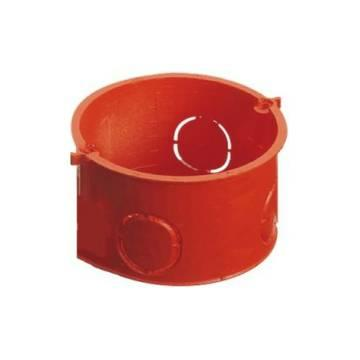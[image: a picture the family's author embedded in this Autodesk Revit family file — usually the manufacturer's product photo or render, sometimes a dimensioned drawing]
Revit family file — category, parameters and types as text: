
# Revit family: Building-ContenitoriIncasso-GEWISS-24SC-SCATOLE-INCASSO_TONDA
name_source: partatom
category: Apparecchi elettrici
revit_build: Autodesk Revit 2016 (Build: 20161004_0715(x64)
units: mm (PartAtom-declared; Revit-internal decimal feet)

## family parameters
Condiviso = Sì
Host = Muro
Mantenere orientamento annotazione = Sì
Numero OmniClass = 23.80.30.14.24
Punto di calcolo locali = Sì
Quota connettore circolare = Usa diametro
Sempre verticale = Sì
Taglio con vuoti quando caricato = Sì
Tipo di parte = Normale
Titolo OmniClass = Junction Boxes

## types (2) — shared parameters
Caratteristiche = Halogen free
Catalogo = BUILDING
Catalogo Serie = 24SC
Codice Electrocod = 0210
Descrizione: = Cilindrica
Diametro = 85 mm  [stored 0.278871 ft]
Diametro interno = 80 mm  [stored 0.262467 ft]
Glow Wire Test = 650°C
IDF = 002cb684-893c-4c20-b679-15194001214f
IDT = e9e05727-a289-4381-9e61-a78239658332
Immagine tipo = GW24210.jpg
Installazione = Incasso
Per Pareti = Muratura
Produttore = GEWISS S.p.A.
Profondità = 42 mm  [stored 0.137795 ft]
Profondità interna = 37 mm  [stored 0.121391 ft]
SEO = Scatola
Scheda Tecnica = https://www.gewiss.com
Temperatura di impiego = -15 +60 °C
Termopressione con biglia = 70 °C
URL = https://www.gewiss.com
Versione file RFA = 19.0

## per-type parameters (varying)
| type | Codice EAN | Descrizione | Dimensioni (mm) | Modello |
| GW24210 - Scatola rotonda cilindrica D. 85mm | 8011564016736 | SCATOLA ROTONDA CILINDRICA D.85 | Ã˜ 85x42 | GW24210 |
| GW24209 - Scatola rotonda cilindrica D. 65mm | 8011564016712 | SCATOLA ROTONDA CILINDRICA D.65 | Ã˜ 65x38 | GW24209 |

note: [stored X ft] marks values corroborated as IEEE doubles in the binary element streams (Revit-internal decimal feet)
